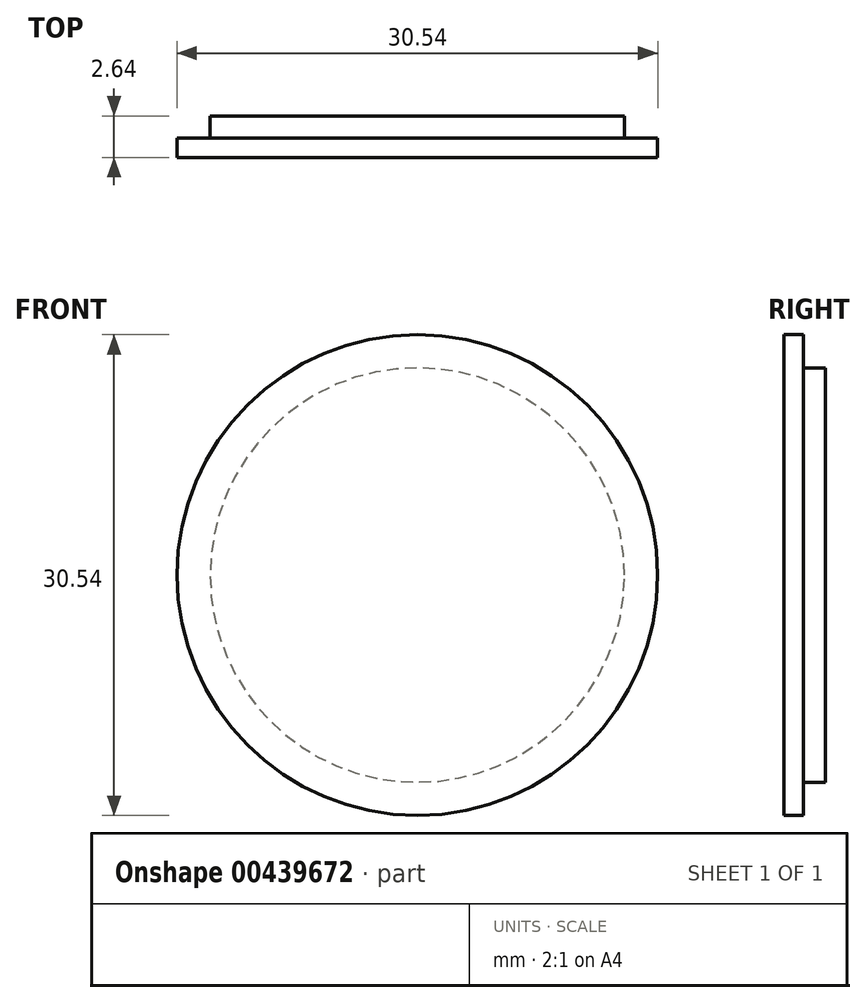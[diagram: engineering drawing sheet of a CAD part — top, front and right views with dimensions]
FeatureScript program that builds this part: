
annotation { "Feature Type Name" : "Feature", "Feature Type Description" : "" }
export const myFeature = defineFeature(function(context is Context, id is Id, definition is map)
    precondition{}
    {
        {
            var Q0;
            Q0=qCreatedBy(makeId("Front.planeOp"),FACE);
            var sketch = newSketch(context, id + "F0", { "sketchPlane" : qUnion([Q0])});
            skCircle(sketch, "E0", {"center": v(0, 0) * mm, "radius": 15.27 * mm});
            skSolve(sketch);
        }
        {
            var Q0;
            Q0 = qSketchRegion(id + "F0", true);
            extrude(context, id + "F1", {"entities" : qUnion([Q0]), "oppositeDirection" : true, "depth" : 1.24 * mm, "offsetDistance" : 25.4 * mm});
        }
        {
            var Q0;
            Q0=makeQuery(id+"F1.opExtrude","CAP_FACE",FACE,{"disambiguationData":[OSD([sQuery(id+"F0.wireOp",EDGE,"E0")])],"isStart":false});
            var sketch = newSketch(context, id + "F2", { "sketchPlane" : qUnion([Q0])});
            skCircle(sketch, "E1", {"center": v(0, 0) * mm, "radius": 13.16 * mm});
            skSolve(sketch);
        }
        {
            var Q0;
            Q0 = qSketchRegion(id + "F2", true);
            extrude(context, id + "F3", {"entities" : qUnion([Q0]), "operationType" : NewBodyOperationType.ADD, "depth" : 1.4 * mm, "offsetDistance" : 25.4 * mm});
        }
    });
